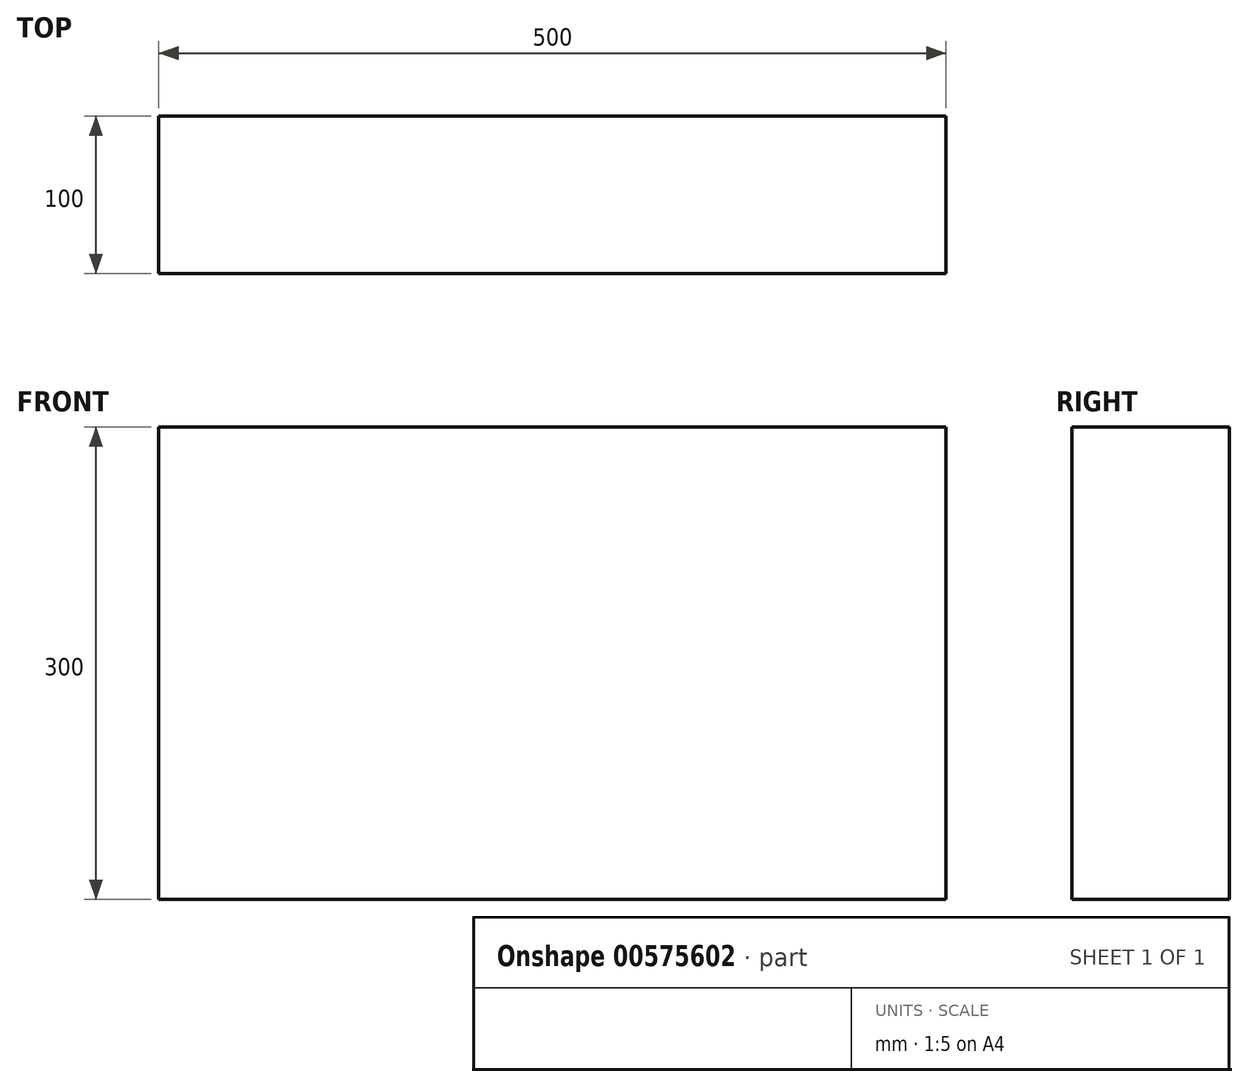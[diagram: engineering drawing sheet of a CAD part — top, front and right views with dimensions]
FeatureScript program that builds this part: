
annotation { "Feature Type Name" : "Feature", "Feature Type Description" : "" }
export const myFeature = defineFeature(function(context is Context, id is Id, definition is map)
    precondition{}
    {
        {
            var Q0;
            Q0=qCreatedBy(makeId("Front.planeOp"),FACE);
            var sketch = newSketch(context, id + "F0", { "sketchPlane" : qUnion([Q0])});
            skLineSegment(sketch, "E0.bottom", {"start": v(250, -150) * mm, "end": v(-250, -150) * mm});
            skLineSegment(sketch, "E0.top", {"start": v(250, 150) * mm, "end": v(-250, 150) * mm});
            skLineSegment(sketch, "E0.left", {"start": v(250, -150) * mm, "end": v(250, 150) * mm});
            skLineSegment(sketch, "E0.right", {"start": v(-250, -150) * mm, "end": v(-250, 150) * mm});
            skPoint(sketch, "E0.middle", {"position": v(0, 0) * mm});
            skSolve(sketch);
        }
        {
            var Q0;
            Q0=makeQuery(id+"F0.imprint","IMPRINT",FACE,{"disambiguationData":[TD([[makeQuery(id+"F0.imprint","IMPRINT",EDGE,{"derivedFrom":sQuery(id+"F0.wireOp",EDGE,"E0.bottom")}),-1.0]])]});
            extrude(context, id + "F1", {"entities" : qUnion([Q0]), "depth" : 100 * mm, "offsetDistance" : 25 * mm});
        }
    });
